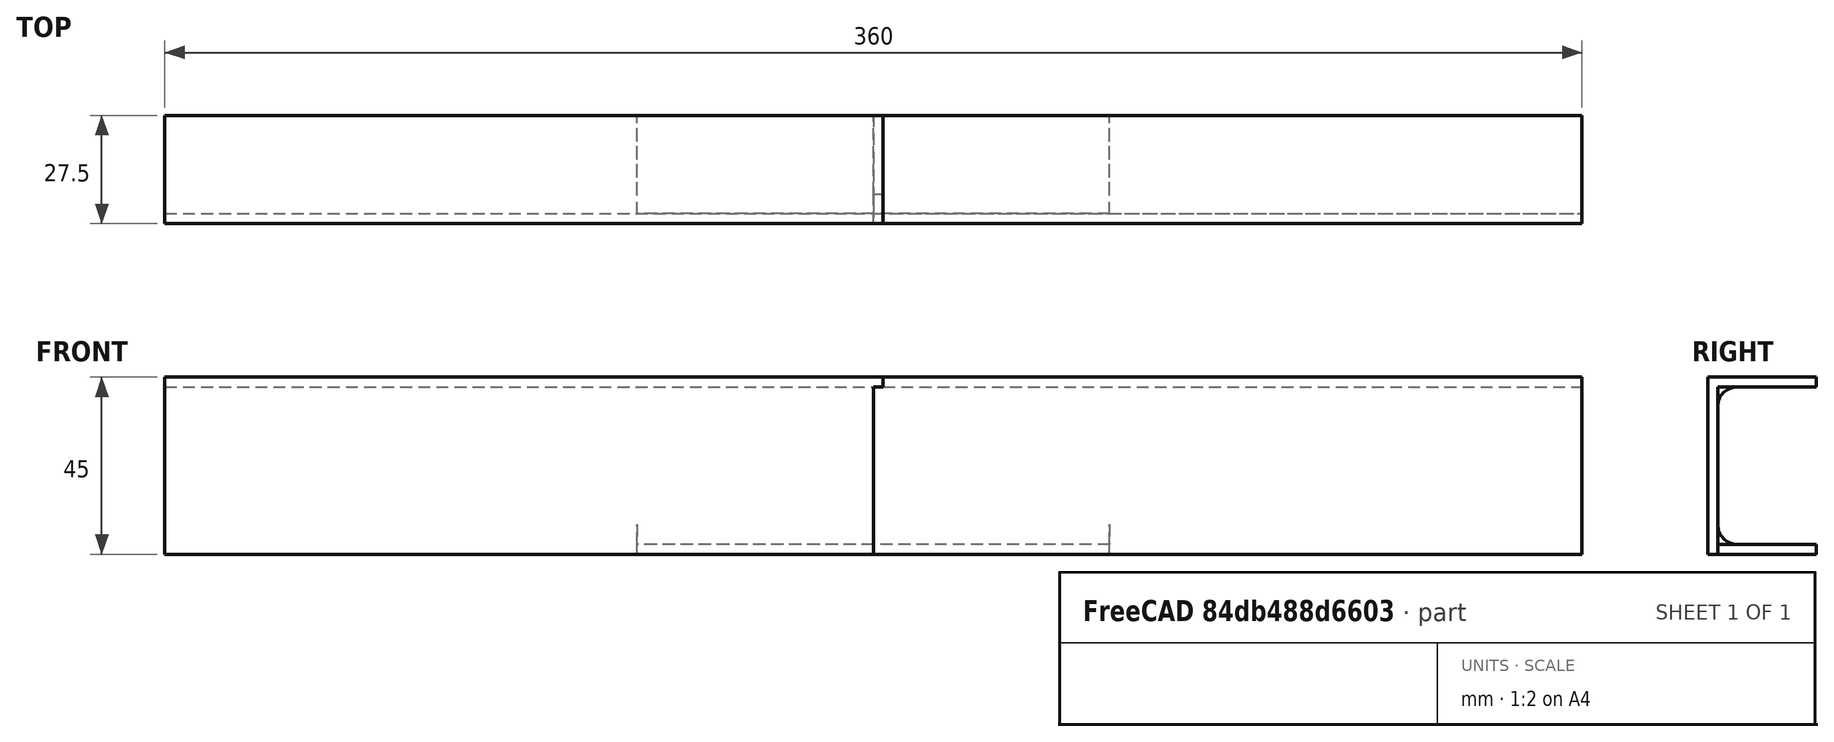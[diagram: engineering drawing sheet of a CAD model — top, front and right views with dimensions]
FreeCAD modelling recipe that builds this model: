
FCSTD DOCUMENT  (FreeCAD 0.17R13522 (Git))
Label: jeder_miklajat
License: CreativeCommons Attribution-ShareAlike
LicenseURL: http://creativecommons.org/licenses/by-sa/4.0/
objects: Part::Box×8, Part::Cut×5, Part::Feature×3, Part::MultiFuse×2, Part::Fillet×2
note: 20 computed .brp shape members not serialized (recipe doc carries the construction recipe); baked Part::Feature solids carry a one-line shape summary decoded from their .brp

FEATURE [Part::Box] Box  label="Cube"
  AttacherType = Attacher::AttachEngine3D
  Height = 2.5
  Length = 120
  Placement = pos=(0,-10,0) rot=(0,0,1;0rad)
  Width = 37.5
FEATURE [Part::Box] Box001  label="Cube001"
  AttacherType = Attacher::AttachEngine3D
  Height = 42.5
  Length = 360
  Placement = pos=(-120,0,0) rot=(0,0,1;0rad)
  Width = 2.5
FEATURE [Part::Box] Box002  label="Cube002"
  AttacherType = Attacher::AttachEngine3D
  Height = 2.5
  Length = 360
  Placement = pos=(-120,0,42.5) rot=(0,0,1;0rad)
  Width = 27.5
FEATURE [Part::MultiFuse] Fusion
  Shapes = -> [Box,Box001]
FEATURE [Part::MultiFuse] Fusion001
  Shapes = -> [Box002,Fusion]
FEATURE [Part::Box] Box003  label="Cube003"
  AttacherType = Attacher::AttachEngine3D
  Height = 10
  Length = 139
  Placement = pos=(-10,-10,-3) rot=(0,0,1;0rad)
  Width = 10
FEATURE [Part::Cut] Cut
  Base = -> Fusion001
  Tool = -> Box003
FEATURE [Part::Feature] Cut001
  shape: bbox 360 x 27.5 x 45 mm, 12 faces (baked)
FEATURE [Part::Fillet] Fillet
  Base = -> Cut001
  Edges = 1 edges r=5: [Edge14]
FEATURE [Part::Fillet] Fillet001
  Base = -> Fillet
  Edges = 1 edges r=5: [Edge8]
FEATURE [Part::Box] Box004  label="Cube004"
  AttacherType = Attacher::AttachEngine3D
  Height = 100
  Length = 360
  Placement = pos=(60,-10,-57.5) rot=(0,0,1;0rad)
  Width = 100
FEATURE [Part::Box] Box005  label="Cube005"
  AttacherType = Attacher::AttachEngine3D
  Height = 100
  Length = 360
  Placement = pos=(62.5,-10,12) rot=(0,0,1;0rad)
  Width = 100
FEATURE [Part::Box] Box006  label="Cube006"
  AttacherType = Attacher::AttachEngine3D
  Height = 100
  Length = 360
  Placement = pos=(-297.5,-10,42.5) rot=(0,0,1;0rad)
  Width = 100
FEATURE [Part::Box] Box007  label="Cube007"
  AttacherType = Attacher::AttachEngine3D
  Height = 100
  Length = 360
  Placement = pos=(-300,-10,-5.5) rot=(0,0,1;0rad)
  Width = 100
FEATURE [Part::Feature] Fillet001001  label="pieza_izquierda"
  shape: bbox 360 x 27.5 x 45 mm, 14 faces (baked)
FEATURE [Part::Feature] Fillet001002  label="pieza_derecha"
  shape: bbox 360 x 27.5 x 45 mm, 14 faces (baked)
FEATURE [Part::Cut] Cut002
  Base = -> Fillet001002
  Tool = -> Box004
FEATURE [Part::Cut] Cut003  label="mikl_derecha"
  Base = -> Cut002
  Tool = -> Box005
FEATURE [Part::Cut] Cut004
  Base = -> Fillet001001
  Tool = -> Box007
FEATURE [Part::Cut] Cut005  label="mikl_izquierda"
  Base = -> Cut004
  Tool = -> Box006
